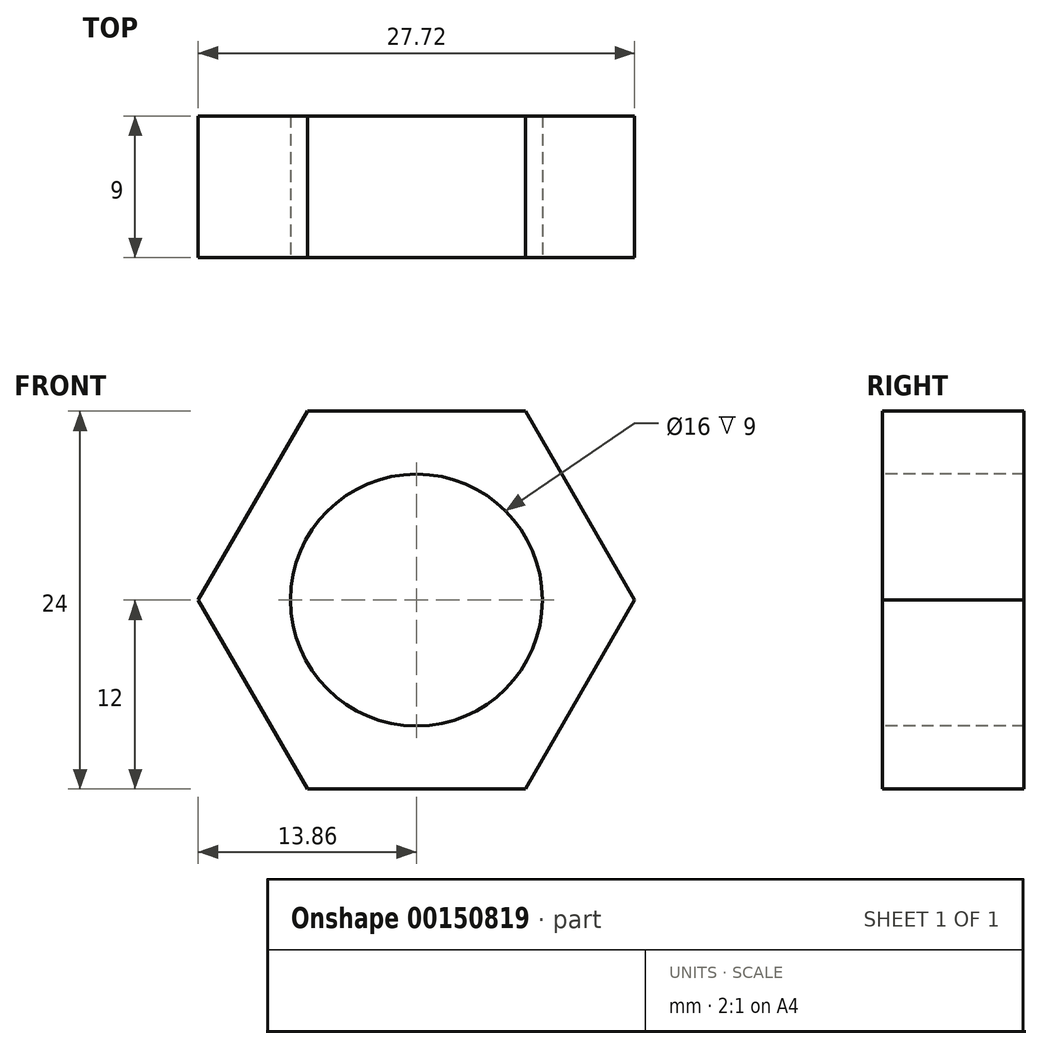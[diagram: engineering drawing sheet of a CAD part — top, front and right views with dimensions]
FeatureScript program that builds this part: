
annotation { "Feature Type Name" : "Feature", "Feature Type Description" : "" }
export const myFeature = defineFeature(function(context is Context, id is Id, definition is map)
    precondition{}
    {
        {
            var Q0;
            Q0=qCreatedBy(makeId("Front.planeOp"),FACE);
            var sketch = newSketch(context, id + "F0", { "sketchPlane" : qUnion([Q0])});
            skCircle(sketch, "E0.cCircle", {"center": v(0, 0) * mm, "radius": 12 * mm, "construction": true});
            skLineSegment(sketch, "E0.0", {"start": v(-6.93, 12) * mm, "end": v(6.93, 12) * mm});
            skLineSegment(sketch, "E0.1", {"start": v(6.93, 12) * mm, "end": v(13.86, 0) * mm});
            skLineSegment(sketch, "E0.2", {"start": v(13.86, 0) * mm, "end": v(6.93, -12) * mm});
            skLineSegment(sketch, "E0.3", {"start": v(6.93, -12) * mm, "end": v(-6.93, -12) * mm});
            skLineSegment(sketch, "E0.4", {"start": v(-6.93, -12) * mm, "end": v(-13.86, 0) * mm});
            skLineSegment(sketch, "E0.5", {"start": v(-13.86, 0) * mm, "end": v(-6.93, 12) * mm});
            skPoint(sketch, "E0.0.midPoint", {"position": v(0, 12) * mm});
            skSolve(sketch);
        }
        {
            var Q0;
            Q0=qSketchRegion(id+"F0",true);
            extrude(context, id + "F1", {"entities" : qUnion([Q0]), "oppositeDirection" : true, "depth" : 9 * mm});
        }
        {
            var Q0;
            Q0=makeQuery(id+"F1.opExtrude","CAP_FACE",FACE,{"disambiguationData":[OSD([sQuery(id+"F0.wireOp",EDGE,"E0.0"),sQuery(id+"F0.wireOp",EDGE,"E0.1"),sQuery(id+"F0.wireOp",EDGE,"E0.2"),sQuery(id+"F0.wireOp",EDGE,"E0.3"),sQuery(id+"F0.wireOp",EDGE,"E0.4"),sQuery(id+"F0.wireOp",EDGE,"E0.5")])],"isStart":true});
            var sketch = newSketch(context, id + "F2", { "sketchPlane" : qUnion([Q0])});
            skCircle(sketch, "E1", {"center": v(0, 0) * mm, "radius": 8 * mm});
            skSolve(sketch);
        }
        {
            var Q0;
            Q0=qSketchRegion(id+"F2",true);
            extrude(context, id + "F3", {"entities" : qUnion([Q0]), "operationType" : NewBodyOperationType.REMOVE, "endBound" : BoundingType.THROUGH_ALL, "oppositeDirection" : true, "depth" : 25 * mm});
        }
    });
